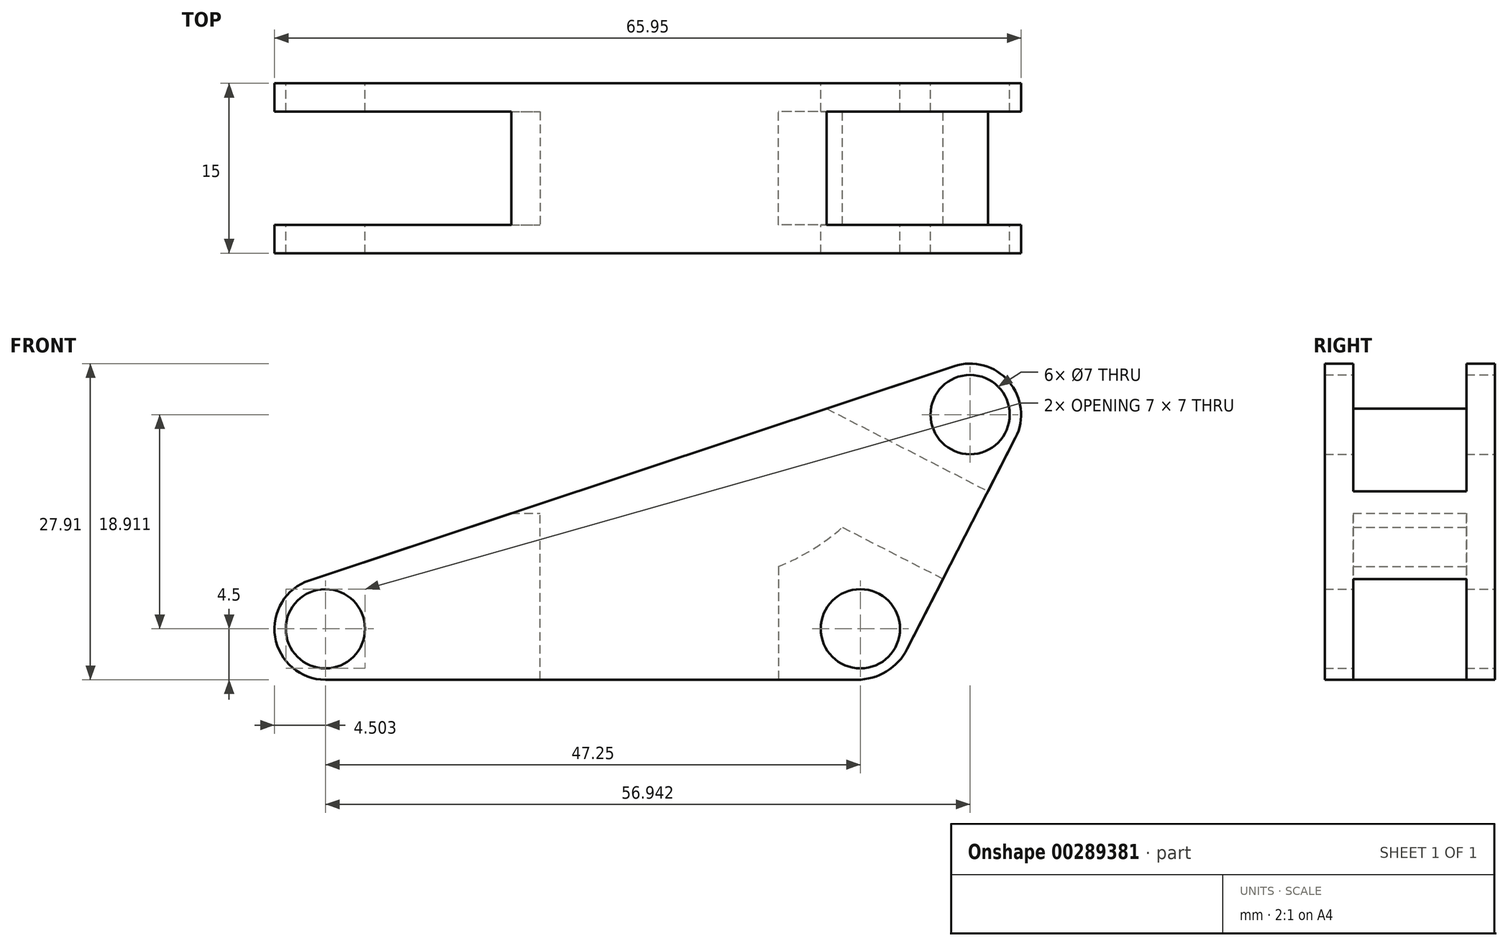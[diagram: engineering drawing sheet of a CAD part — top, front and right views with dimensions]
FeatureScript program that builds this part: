
annotation { "Feature Type Name" : "Feature", "Feature Type Description" : "" }
export const myFeature = defineFeature(function(context is Context, id is Id, definition is map)
    precondition{}
    {
        {
            var Q0;
            Q0=qCreatedBy(makeId("Front.planeOp"),FACE);
            var sketch = newSketch(context, id + "F0", { "sketchPlane" : qUnion([Q0])});
            skLineSegment(sketch, "E0", {"start": v(-11.38, 0) * mm, "end": v(38.62, 0) * mm});
            skArc(sketch, "E1", {"start": v(-11.38, 0) * mm, "mid": v(-15.82, 3.78) * mm, "end": v(-12.8, 8.77) * mm});
            skLineSegment(sketch, "E2", {"start": v(38.62, 0) * mm, "end": v(49.57, 21.36) * mm});
            skArc(sketch, "E3", {"start": v(49.57, 21.36) * mm, "mid": v(48.98, 26.34) * mm, "end": v(44.15, 27.68) * mm});
            skLineSegment(sketch, "E4", {"start": v(-12.8, 8.77) * mm, "end": v(44.15, 27.68) * mm});
            skCircle(sketch, "E5", {"center": v(-11.38, 4.5) * mm, "radius": 3.5 * mm});
            skCircle(sketch, "E6", {"center": v(45.57, 23.41) * mm, "radius": 3.5 * mm});
            skCircle(sketch, "E7", {"center": v(35.87, 4.5) * mm, "radius": 3.5 * mm});
            skSolve(sketch);
        }
        {
            var Q0;
            Q0=makeQuery(id+"F0.imprint","IMPRINT",FACE,{"disambiguationData":[TD([[makeQuery(id+"F0.imprint","IMPRINT",EDGE,{"derivedFrom":sQuery(id+"F0.wireOp",EDGE,"E0")}),1.0]])]});
            extrude(context, id + "F1", {"entities" : qUnion([Q0]), "endBound" : BoundingType.SYMMETRIC, "depth" : 15 * mm});
        }
        {
            var Q0;
            Q0=makeQuery(id+"F1.opExtrude","SWEPT_FACE",FACE,{"disambiguationData":[OSD([sQuery(id+"F0.wireOp",EDGE,"E2")])]});
            var sketch = newSketch(context, id + "F2", { "sketchPlane" : qUnion([Q0])});
            skLineSegment(sketch, "E8.bottom", {"start": v(-5, 17.62) * mm, "end": v(5, 17.62) * mm});
            skLineSegment(sketch, "E8.top", {"start": v(-5, 27.62) * mm, "end": v(5, 27.62) * mm});
            skLineSegment(sketch, "E8.left", {"start": v(-5, 17.62) * mm, "end": v(-5, 27.62) * mm});
            skLineSegment(sketch, "E8.right", {"start": v(5, 17.62) * mm, "end": v(5, 27.62) * mm});
            skSolve(sketch);
        }
        {
            var Q0;
            Q0 = qSketchRegion(id + "F2", true);
            extrude(context, id + "F3", {"entities" : qUnion([Q0]), "operationType" : NewBodyOperationType.REMOVE, "oppositeDirection" : true, "depth" : 10 * mm});
        }
        {
            var Q0;
            Q0=makeQuery(id+"F1.opExtrude","SWEPT_FACE",FACE,{"disambiguationData":[OSD([sQuery(id+"F0.wireOp",EDGE,"E0")])]});
            var sketch = newSketch(context, id + "F4", { "sketchPlane" : qUnion([Q0])});
            skLineSegment(sketch, "E9.bottom", {"start": v(38.62, 5) * mm, "end": v(28.62, 5) * mm});
            skLineSegment(sketch, "E9.top", {"start": v(38.62, -5) * mm, "end": v(28.62, -5) * mm});
            skLineSegment(sketch, "E9.left", {"start": v(38.62, 5) * mm, "end": v(38.62, -5) * mm});
            skLineSegment(sketch, "E9.right", {"start": v(28.62, 5) * mm, "end": v(28.62, -5) * mm});
            skSolve(sketch);
        }
        {
            var Q0;
            Q0=makeQuery(id+"F4.imprint","IMPRINT",FACE,{"disambiguationData":[TD([[makeQuery(id+"F4.imprint","IMPRINT",EDGE,{"derivedFrom":sQuery(id+"F4.wireOp",EDGE,"E9.bottom")}),1.0]])]});
            extrude(context, id + "F5", {"entities" : qUnion([Q0]), "operationType" : NewBodyOperationType.REMOVE, "oppositeDirection" : true, "depth" : 10 * mm});
        }
        {
            var Q0;
            Q0=makeQuery(id+"F5.boolean.opBoolean","INTERSECT",EDGE,{"derivedFrom":[makeQuery(id+"F3.boolean.opBoolean","COPY",FACE,{"derivedFrom":makeQuery(id+"F3.opExtrude","CAP_FACE",FACE,{"disambiguationData":[OSD([sQuery(id+"F2.wireOp",EDGE,"E8.bottom"),sQuery(id+"F2.wireOp",EDGE,"E8.top"),sQuery(id+"F2.wireOp",EDGE,"E8.left"),sQuery(id+"F2.wireOp",EDGE,"E8.right")])],"isStart":false})}),makeQuery(id+"F5.opExtrude","CAP_FACE",FACE,{"disambiguationData":[OSD([sQuery(id+"F4.wireOp",EDGE,"E9.bottom"),sQuery(id+"F4.wireOp",EDGE,"E9.top"),sQuery(id+"F4.wireOp",EDGE,"E9.left"),sQuery(id+"F4.wireOp",EDGE,"E9.right")])],"isStart":false})]});
            fillet(context, id + "F6", {"entities" : qUnion([Q0]), "radius" : 19.2 * mm, "tangentPropagation" : true, "allowEdgeOverflow" : false});
        }
        {
            var Q0;
            Q0=qCreatedBy(makeId("Right.planeOp"),FACE);
            var sketch = newSketch(context, id + "F7", { "sketchPlane" : qUnion([Q0])});
            skLineSegment(sketch, "E10.bottom", {"start": v(5, 0) * mm, "end": v(-5, 0) * mm});
            skLineSegment(sketch, "E10.top", {"start": v(5, 14.7) * mm, "end": v(-5, 14.7) * mm});
            skLineSegment(sketch, "E10.left", {"start": v(5, 0) * mm, "end": v(5, 14.7) * mm});
            skLineSegment(sketch, "E10.right", {"start": v(-5, 0) * mm, "end": v(-5, 14.7) * mm});
            skSolve(sketch);
        }
        {
            var Q0;
            Q0 = qSketchRegion(id + "F7", true);
            extrude(context, id + "F8", {"entities" : qUnion([Q0]), "operationType" : NewBodyOperationType.REMOVE, "endBound" : BoundingType.SYMMETRIC, "oppositeDirection" : true, "depth" : 35.2 * mm});
        }
        {
            var Q0;
            Q0=makeQuery(id+"F8.boolean.opBoolean","COPY",FACE,{"derivedFrom":makeQuery(id+"F8.opExtrude","CAP_FACE",FACE,{"disambiguationData":[OSD([sQuery(id+"F7.wireOp",EDGE,"E10.bottom"),sQuery(id+"F7.wireOp",EDGE,"E10.top"),sQuery(id+"F7.wireOp",EDGE,"E10.left"),sQuery(id+"F7.wireOp",EDGE,"E10.right")])],"isStart":true})});
            extrude(context, id + "F9", {"entities" : qUnion([Q0]), "operationType" : NewBodyOperationType.ADD, "depth" : 10 * mm});
        }
        {
            var Q0;
            Q0=makeQuery(id+"F1.opExtrude","SWEPT_FACE",FACE,{"disambiguationData":[OSD([sQuery(id+"F0.wireOp",EDGE,"E2")])]});
            var sketch = newSketch(context, id + "F10", { "sketchPlane" : qUnion([Q0])});
            skLineSegment(sketch, "E11.bottom", {"start": v(-5, 46.31) * mm, "end": v(5, 46.31) * mm});
            skLineSegment(sketch, "E11.top", {"start": v(-5, 36.31) * mm, "end": v(5, 36.31) * mm});
            skLineSegment(sketch, "E11.left", {"start": v(-5, 46.31) * mm, "end": v(-5, 36.31) * mm});
            skLineSegment(sketch, "E11.right", {"start": v(5, 46.31) * mm, "end": v(5, 36.31) * mm});
            skSolve(sketch);
        }
        {
            var Q0;
            Q0 = qSketchRegion(id + "F10", true);
            extrude(context, id + "F11", {"entities" : qUnion([Q0]), "operationType" : NewBodyOperationType.REMOVE, "oppositeDirection" : true, "depth" : 25 * mm});
        }
        {
            var Q0;
            {var subQ0=sQuery(id+"F0.wireOp",EDGE,"E2");var subQ1=sQuery(id+"F0.wireOp",EDGE,"E0");Q0=makeQuery(id+"F3.boolean.opBoolean","SPLIT",EDGE,{"disambiguationData":[TD([makeQuery(id+"F3.opExtrude","SWEPT_FACE",FACE,{"disambiguationData":[OSD([sQuery(id+"F2.wireOp",EDGE,"E8.right")])]})])],"derivedFrom":makeQuery(id+"F1.opExtrude","SWEPT_EDGE",EDGE,{"disambiguationData":[OSD([subQ1,subQ0])]})});}
            fillet(context, id + "F12", {"entities" : qUnion([Q0]), "radius" : 5 * mm, "tangentPropagation" : true, "allowEdgeOverflow" : false});
        }
        {
            var Q0;
            {var subQ0=sQuery(id+"F0.wireOp",EDGE,"E2");var subQ1=sQuery(id+"F0.wireOp",EDGE,"E0");Q0=makeQuery(id+"F3.boolean.opBoolean","SPLIT",EDGE,{"disambiguationData":[TD([makeQuery(id+"F3.opExtrude","SWEPT_FACE",FACE,{"disambiguationData":[OSD([sQuery(id+"F2.wireOp",EDGE,"E8.left")])]})])],"derivedFrom":makeQuery(id+"F1.opExtrude","SWEPT_EDGE",EDGE,{"disambiguationData":[OSD([subQ1,subQ0])]})});}
            fillet(context, id + "F13", {"entities" : qUnion([Q0]), "radius" : 5 * mm, "tangentPropagation" : true, "allowEdgeOverflow" : false});
        }
    });
